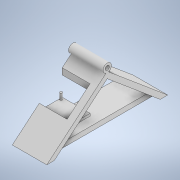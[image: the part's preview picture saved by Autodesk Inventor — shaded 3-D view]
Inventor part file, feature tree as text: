
AUTODESK INVENTOR PART (.ipt)
format: ipt  version: 2021 (Build 250183000, 183)  size: 221,696 bytes
history: native  units: mm
features: extrude x11, sketch x10, projected_geometry x6, plane x1
ambient origin geometry x8: Origin, YZ Plane, XZ Plane, XY Plane, X Axis, Y Axis, Z Axis, Center Point
bodies: Volumenkörper1 (feature_tree)
feature tree (28):
  extrude  "Extrusion1"  Depth=3.5mm
  extrude  "Extrusion2"  Depth=2.0mm
  extrude  "Extrusion3"  Depth=28.5mm TaperAngle=0.0deg
  extrude  "Extrusion4"  Depth=24.0mm TaperAngle=0.0deg
  extrude  "Extrusion5"  TaperAngle=0.0deg  [1 undecoded]
  plane  "Arbeitsebene1"
  extrude  "Extrusion6"  [1 undecoded]
  extrude  "Extrusion7"  Depth=3.5mm TaperAngle=0.0deg
  extrude  "Extrusion8"  TaperAngle=0.0deg  [1 undecoded]
  extrude  "Extrusion9"  Depth=4.0mm TaperAngle=0.0deg
  sketch  "Skizze10"  dims[d26=2.0mm d27=19.0mm d28=10.0mm d29=0.0mm d30=2.0mm d31=15.0mm d32=2.0mm d34=0.0mm d35=0.0mm d36=5.0mm d37=0.0mm d38=7.5mm d39=1.0mm]
  extrude  "Extrusion10"  Depth=19.0mm
  extrude  "Extrusion11"  Depth=10.0mm TaperAngle=0.0deg
  sketch  "Skizze1"  dims[d0=6.981317mm d1=3.5mm]
  sketch  "Skizze2"  dims[d2=7.0mm d3=2.0mm]
  projected_geometry  "Projizierte Kontur1"
  sketch  "Skizze3"  dims[d4=100.0mm d5=28.5mm d6=0.0mm]
  projected_geometry  "Projizierte Kontur2"
  sketch  "Skizze4"  dims[d7=5.0mm d8=0.0mm d9=24.0mm d10=0.0mm]
  sketch  "Skizze5"  dims[d11=72.5mm d12=0.0mm d13=0.0mm]
  projected_geometry  "Projizierte Kontur3"
  sketch  "Skizze6"  dims[d14=14.5mm d15=0.0mm d16=-2.0mm]
  sketch  "Skizze7"  dims[d17=2.0mm d18=3.5mm d19=0.0mm]
  projected_geometry  "Projizierte Kontur4"
  sketch  "Skizze8"  dims[d20=2.0mm d21=0.0mm d22=0.0mm]
  sketch  "Skizze9"  dims[d23=4.0mm d24=15.0mm d25=0.0mm]
  projected_geometry  "Projizierte Kontur5"
  projected_geometry  "Projizierte Kontur6"
note: 3 required parameter values undecoded (feature->parameter linkage not recoverable at this tier; creation-order binding heuristic only, values carry confidence <= 0.55)
